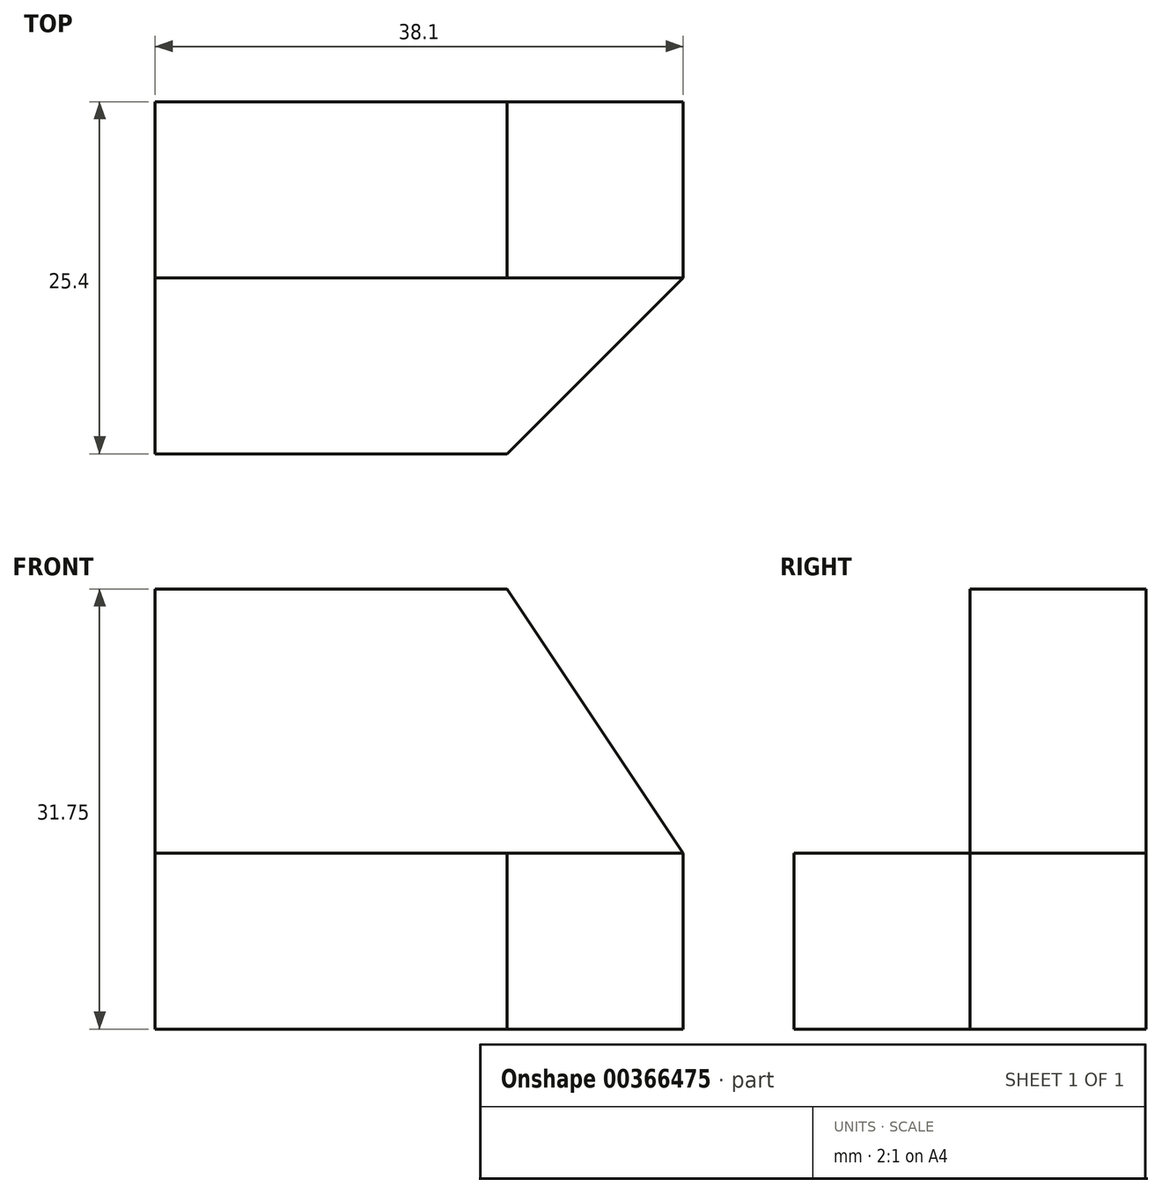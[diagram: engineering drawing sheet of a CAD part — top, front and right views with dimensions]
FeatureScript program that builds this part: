
annotation { "Feature Type Name" : "Feature", "Feature Type Description" : "" }
export const myFeature = defineFeature(function(context is Context, id is Id, definition is map)
    precondition{}
    {
        {
            var Q0;
            Q0=qCreatedBy(makeId("Right.planeOp"),FACE);
            var sketch = newSketch(context, id + "F0", { "sketchPlane" : qUnion([Q0])});
            skLineSegment(sketch, "E0", {"start": v(0, 0) * mm, "end": v(0, 31.75) * mm});
            skLineSegment(sketch, "E1", {"start": v(0, 0) * mm, "end": v(-25.4, 0) * mm});
            skLineSegment(sketch, "E2", {"start": v(-25.4, 0) * mm, "end": v(-25.4, 12.7) * mm});
            skLineSegment(sketch, "E3", {"start": v(0, 31.75) * mm, "end": v(-12.7, 31.75) * mm});
            skLineSegment(sketch, "E4", {"start": v(-25.4, 12.7) * mm, "end": v(-12.7, 12.7) * mm});
            skPoint(sketch, "E5.end.orphan", {"position": v(-12.7, 13.82) * mm});
            skLineSegment(sketch, "E6", {"start": v(-12.7, 12.7) * mm, "end": v(-12.7, 31.75) * mm});
            skSolve(sketch);
        }
        {
            var Q0;
            Q0 = qSketchRegion(id + "F0", true);
            extrude(context, id + "F1", {"entities" : qUnion([Q0]), "depth" : 38.1 * mm});
        }
        {
            var Q0;
            Q0=makeQuery(id+"F1.opExtrude","SWEPT_FACE",FACE,{"disambiguationData":[OSD([sQuery(id+"F0.wireOp",EDGE,"E6")])]});
            var sketch = newSketch(context, id + "F2", { "sketchPlane" : qUnion([Q0])});
            skLineSegment(sketch, "E7", {"start": v(0, 31.75) * mm, "end": v(25.4, 31.75) * mm});
            skLineSegment(sketch, "E8", {"start": v(25.4, 31.75) * mm, "end": v(38.1, 12.7) * mm});
            skSolve(sketch);
        }
        {
            var Q0;
            Q0 = qSketchRegion(id + "F2", true);
            var Q1;
            {var subQ0=sQuery(id+"F2.wireOp",EDGE,"E8");Q1=makeQuery(id+"F2.imprint","IMPRINT",FACE,{"disambiguationData":[TD([[makeQuery(id+"F2.imprint","IMPRINT",EDGE,{"derivedFrom":subQ0}),1.0]])]});}
            extrude(context, id + "F3", {"entities" : qUnion([Q0, Q1]), "operationType" : NewBodyOperationType.REMOVE, "oppositeDirection" : true, "depth" : 25.4 * mm});
        }
        {
            var Q0;
            Q0=makeQuery(id+"F1.opExtrude","SWEPT_FACE",FACE,{"disambiguationData":[OSD([sQuery(id+"F0.wireOp",EDGE,"E4")])]});
            var sketch = newSketch(context, id + "F4", { "sketchPlane" : qUnion([Q0])});
            skLineSegment(sketch, "E9", {"start": v(0, -25.4) * mm, "end": v(25.4, -25.4) * mm});
            skLineSegment(sketch, "E10", {"start": v(25.4, -25.4) * mm, "end": v(38.1, -12.7) * mm});
            skSolve(sketch);
        }
        {
            var Q0;
            Q0 = qSketchRegion(id + "F4", true);
            var Q1;
            {var subQ0=sQuery(id+"F4.wireOp",EDGE,"E10");Q1=makeQuery(id+"F4.imprint","IMPRINT",FACE,{"disambiguationData":[TD([[makeQuery(id+"F4.imprint","IMPRINT",EDGE,{"derivedFrom":subQ0}),-1.0]])]});}
            extrude(context, id + "F5", {"entities" : qUnion([Q0, Q1]), "operationType" : NewBodyOperationType.REMOVE, "oppositeDirection" : true, "depth" : 25.4 * mm});
        }
    });
